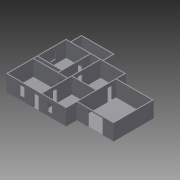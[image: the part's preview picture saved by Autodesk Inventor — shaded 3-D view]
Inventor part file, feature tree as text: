
AUTODESK INVENTOR PART (.ipt)
format: ipt  version: 2013 SP2 (Build 170200200, 200)  size: 348,160 bytes
history: native  units: in
note: dims shown in document units (in); Inventor stores cm internally (conversion verified against a paired STEP export)
features: extrude x9, sketch x4, projected_geometry x2
ambient origin geometry x8: Origin, YZ Plane, XZ Plane, XY Plane, X Axis, Y Axis, Z Axis, Center Point
bodies: Solid1 (feature_tree)
feature tree (15):
  extrude  "Extrusion1"  Depth=6.0in
  extrude  "Extrusion2"  Depth=6.0in
  sketch  "Sketch3"  dims[d5=262.0in d6=240.0in d7=59.0in d8=6.0in]
  extrude  "Extrusion3"  Depth=6.0in
  extrude  "Extrusion4"  Depth=145.0in
  extrude  "Extrusion5"  Depth=6.0in
  extrude  "Extrusion6"  Depth=6.0in
  extrude  "Extrusion7"  Depth=6.0in
  extrude  "Extrusion8"  Depth=72.0in
  extrude  "Extrusion10"  Depth=6.0in
  sketch  "Sketch2"  dims[d0=392.0in d2=392.0in d3=6.0in d4=6.0in]
  projected_geometry  "Projected Loop1"
  projected_geometry  "Projected Loop2"
  sketch  "Sketch4"  dims[d9=6.0in d10=6.0in]
  sketch  "Sketch6"  dims[d11=71.0in d12=29.0in d13=145.0in d14=6.0in d15=6.0in d16=6.0in d17=72.0in d18=6.0in d19=60.0in d20=392.0in d21=6.0in d22=392.0in d23=147.0in d24=72.0in d25=72.0in d26=262.0in d27=6.0in d28=180.0in d29=32.0in d30=392.0in d31=6.0in d32=6.0in d33=162.0in d34=182.0in d35=67.0in d36=98.0in d37=162.0in d38=216.0in d39=6.0in d40=6.0in d41=182.0in d42=6.0in d43=240.0in d44=98.0in d45=128.0in d46=6.0in d47=208.0in d48=32.0in d49=32.0in d51=6.0in d52=70.0in d53=100.0in d56=176.0in d57=32.0in d58=208.0in d59=6.0in d60=6.0in d61=6.0in d62=208.0in d63=155.0in d64=168.0in d65=6.0in d66=102.0in d67=0.0in d68=1.0in d69=0.0in d70=22.0in d71=0.0in d72=21.0in d73=0.0in d74=23.0in d75=0.0in d76=7.0in d77=0.0in d78=21.0in d79=0.0in d80=19.0in d81=25.0in d82=88.0in d83=32.0in d84=25.0in d85=23.0in d86=91.0in d87=29.0in d88=21.0in d89=0.0in d97=36.0in d98=54.0in d99=25.0in d100=79.0in d101=1.0in d102=0.0in]
